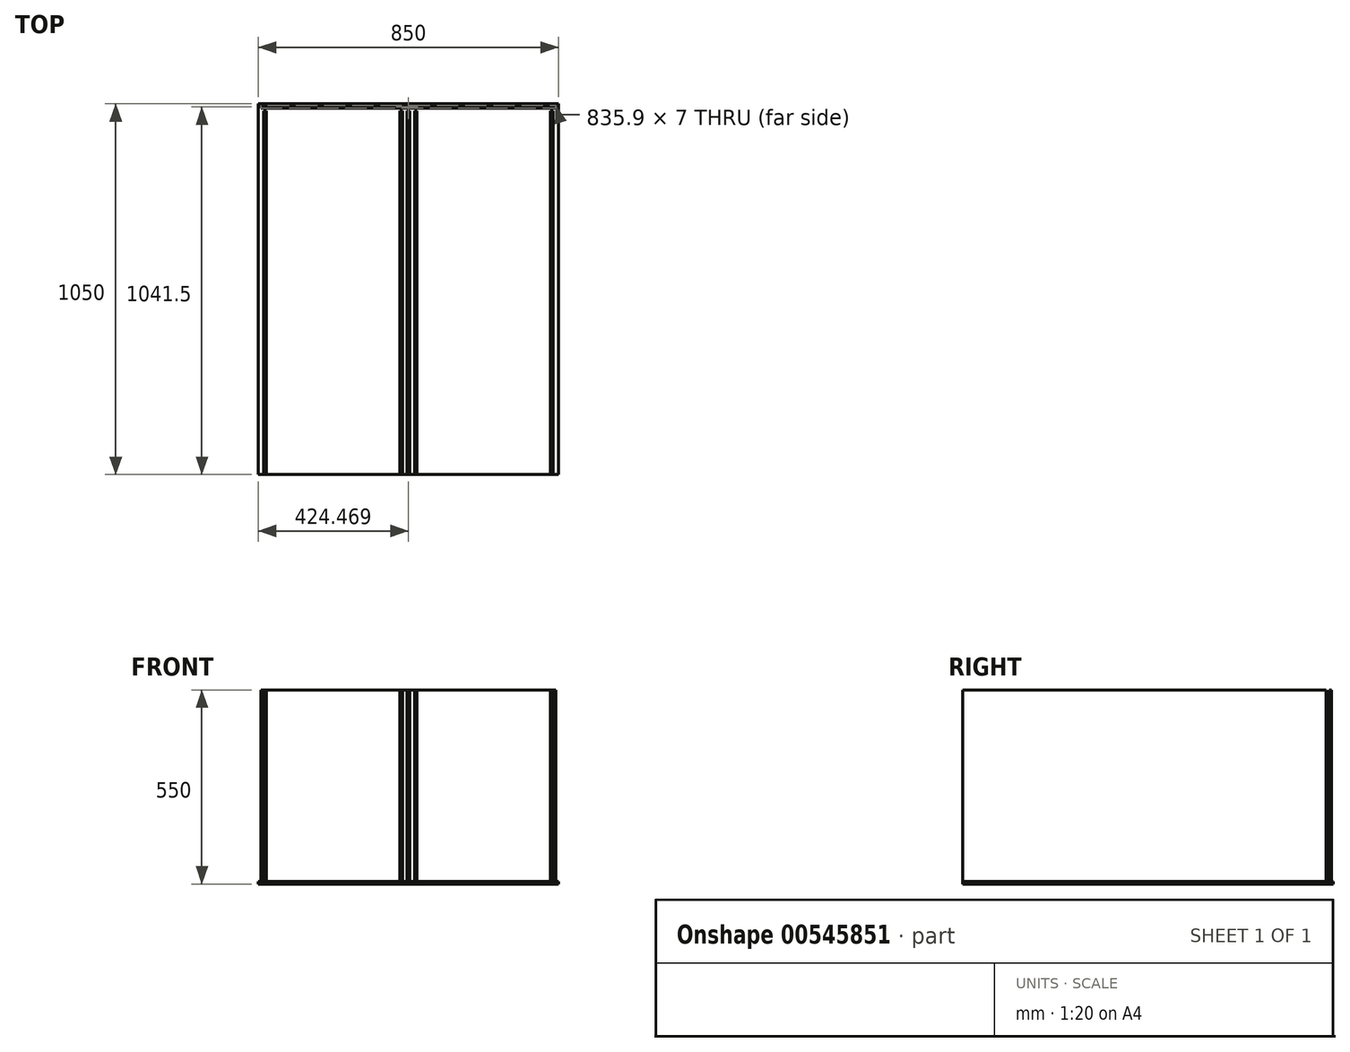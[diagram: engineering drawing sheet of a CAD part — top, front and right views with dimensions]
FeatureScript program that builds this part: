
annotation { "Feature Type Name" : "Feature", "Feature Type Description" : "" }
export const myFeature = defineFeature(function(context is Context, id is Id, definition is map)
    precondition{}
    {
        {
            var Q0;
            Q0=qCreatedBy(makeId("Top.planeOp"),FACE);
            var sketch = newSketch(context, id + "F0", { "sketchPlane" : qUnion([Q0])});
            skLineSegment(sketch, "E0", {"start": v(0, 0) * mm, "end": v(0, -1700) * mm, "construction": true});
            skLineSegment(sketch, "E1", {"start": v(0, -1700) * mm, "end": v(-425, -1700) * mm, "construction": true});
            skLineSegment(sketch, "E2", {"start": v(-675, 0) * mm, "end": v(0, 0) * mm, "construction": true});
            skLineSegment(sketch, "E3", {"start": v(-675, -1200) * mm, "end": v(-675, -1700) * mm, "construction": true});
            skLineSegment(sketch, "E4", {"start": v(-675, -1700) * mm, "end": v(-425, -1700) * mm, "construction": true});
            skLineSegment(sketch, "E5.MirrorCS", {"start": v(675, 0) * mm, "end": v(0, 0) * mm, "construction": true});
            skLineSegment(sketch, "E6.MirrorCS", {"start": v(0, -1700) * mm, "end": v(425, -1700) * mm, "construction": true});
            skLineSegment(sketch, "E7", {"start": v(-425, -1700) * mm, "end": v(-675, -1200) * mm, "construction": true});
            skLineSegment(sketch, "E8", {"start": v(675, 0) * mm, "end": v(675, -1200) * mm, "construction": true});
            skLineSegment(sketch, "E9", {"start": v(425, -1700) * mm, "end": v(-425, -1700) * mm});
            skLineSegment(sketch, "E10", {"start": v(675, -1200) * mm, "end": v(425, -1700) * mm, "construction": true});
            skLineSegment(sketch, "E11", {"start": v(-675, -1200) * mm, "end": v(-675, 0) * mm, "construction": true});
            skLineSegment(sketch, "E12", {"start": v(-425, -650) * mm, "end": v(0, -650) * mm, "construction": true});
            skLineSegment(sketch, "E13.MirrorCS", {"start": v(425, -650) * mm, "end": v(0, -650) * mm, "construction": true});
            skLineSegment(sketch, "E14", {"start": v(-425, -650) * mm, "end": v(-425, -1700) * mm, "construction": true});
            skLineSegment(sketch, "E15", {"start": v(425, -650) * mm, "end": v(425, -1700) * mm, "construction": true});
            skLineSegment(sketch, "E16", {"start": v(-675, -1200) * mm, "end": v(-675, -1700) * mm});
            skLineSegment(sketch, "E17", {"start": v(-425, -1700) * mm, "end": v(-425, -1200) * mm});
            skLineSegment(sketch, "E18", {"start": v(-425, -1200) * mm, "end": v(-675, -1200) * mm});
            skLineSegment(sketch, "E19.MirrorCS", {"start": v(425, -1200) * mm, "end": v(675, -1200) * mm});
            skLineSegment(sketch, "E20.MirrorCS", {"start": v(425, -1700) * mm, "end": v(425, -1200) * mm});
            skLineSegment(sketch, "E21.MirrorCS", {"start": v(675, -1700) * mm, "end": v(425, -1700) * mm, "construction": true});
            skLineSegment(sketch, "E22.MirrorCS", {"start": v(675, -1200) * mm, "end": v(675, -1700) * mm, "construction": true});
            skLineSegment(sketch, "E23", {"start": v(-380, -800) * mm, "end": v(-380, -1630) * mm, "construction": true});
            skLineSegment(sketch, "E24", {"start": v(-30, -800) * mm, "end": v(-30, -1630) * mm, "construction": true});
            skLineSegment(sketch, "E25", {"start": v(-380, -800) * mm, "end": v(-30, -800) * mm, "construction": true});
            skLineSegment(sketch, "E26", {"start": v(-380, -1630) * mm, "end": v(-30, -1630) * mm, "construction": true});
            skLineSegment(sketch, "E27.MirrorCS", {"start": v(380, -800) * mm, "end": v(30, -800) * mm, "construction": true});
            skLineSegment(sketch, "E28.MirrorCS", {"start": v(30, -800) * mm, "end": v(30, -1630) * mm, "construction": true});
            skLineSegment(sketch, "E29.bottom", {"start": v(-24, -670) * mm, "end": v(-17, -670) * mm});
            skLineSegment(sketch, "E29.top", {"start": v(-24, -1700) * mm, "end": v(-17, -1700) * mm});
            skLineSegment(sketch, "E29.left", {"start": v(-17, -670) * mm, "end": v(-17, -1700) * mm});
            skLineSegment(sketch, "E29.right", {"start": v(-24, -670) * mm, "end": v(-24, -1700) * mm});
            skLineSegment(sketch, "E30.bottom", {"start": v(-403, -1700) * mm, "end": v(-410, -1700) * mm});
            skLineSegment(sketch, "E30.top", {"start": v(-403, -670) * mm, "end": v(-410, -670) * mm});
            skLineSegment(sketch, "E30.left", {"start": v(-403, -1700) * mm, "end": v(-403, -670) * mm});
            skLineSegment(sketch, "E30.right", {"start": v(-410, -1700) * mm, "end": v(-410, -670) * mm});
            skLineSegment(sketch, "E31.bottom", {"start": v(-418.48, -662) * mm, "end": v(417.42, -662) * mm});
            skLineSegment(sketch, "E31.top", {"start": v(-418.48, -655) * mm, "end": v(417.42, -655) * mm});
            skLineSegment(sketch, "E31.left", {"start": v(-418.48, -662) * mm, "end": v(-418.48, -655) * mm});
            skLineSegment(sketch, "E31.right", {"start": v(417.42, -662) * mm, "end": v(417.42, -655) * mm});
            skLineSegment(sketch, "E32.MirrorCS", {"start": v(17, -670) * mm, "end": v(17, -1700) * mm});
            skLineSegment(sketch, "E33.MirrorCS", {"start": v(24, -670) * mm, "end": v(24, -1700) * mm});
            skLineSegment(sketch, "E34.MirrorCS", {"start": v(24, -670) * mm, "end": v(17, -670) * mm});
            skLineSegment(sketch, "E35.MirrorCS", {"start": v(403, -670) * mm, "end": v(410, -670) * mm});
            skLineSegment(sketch, "E36.MirrorCS", {"start": v(403, -1700) * mm, "end": v(403, -670) * mm});
            skLineSegment(sketch, "E37.MirrorCS", {"start": v(410, -1700) * mm, "end": v(410, -670) * mm});
            skLineSegment(sketch, "E38.bottom", {"start": v(-3.5, -1700) * mm, "end": v(3.5, -1700) * mm});
            skLineSegment(sketch, "E38.top", {"start": v(-3.5, -670) * mm, "end": v(3.5, -670) * mm});
            skLineSegment(sketch, "E38.left", {"start": v(-3.5, -1700) * mm, "end": v(-3.5, -670) * mm});
            skLineSegment(sketch, "E38.right", {"start": v(3.5, -1700) * mm, "end": v(3.5, -670) * mm});
            skLineSegment(sketch, "E39.bottom", {"start": v(-425, -1700) * mm, "end": v(425, -1700) * mm});
            skLineSegment(sketch, "E39.top", {"start": v(-425, -650) * mm, "end": v(425, -650) * mm});
            skLineSegment(sketch, "E39.left", {"start": v(-425, -1700) * mm, "end": v(-425, -650) * mm});
            skLineSegment(sketch, "E39.right", {"start": v(425, -1700) * mm, "end": v(425, -650) * mm});
            skSolve(sketch);
        }
        {
            var Q0;
            Q0=makeQuery(id+"F0.imprint","IMPRINT",FACE,{"disambiguationData":[TD([[makeQuery(id+"F0.imprint","IMPRINT",EDGE,{"derivedFrom":sQuery(id+"F0.wireOp",EDGE,"E35.MirrorCS")}),-1.0]])]});
            var Q1;
            {var subQ0=sQuery(id+"F0.wireOp",EDGE,"E32.MirrorCS");Q1=makeQuery(id+"F0.imprint","IMPRINT",FACE,{"disambiguationData":[TD([[makeQuery(id+"F0.imprint","IMPRINT",EDGE,{"derivedFrom":subQ0}),1.0]])]});}
            var Q2;
            Q2=makeQuery(id+"F0.imprint","IMPRINT",FACE,{"disambiguationData":[TD([[makeQuery(id+"F0.imprint","IMPRINT",EDGE,{"derivedFrom":sQuery(id+"F0.wireOp",EDGE,"E38.top")}),-1.0]])]});
            var Q3;
            Q3=makeQuery(id+"F0.imprint","IMPRINT",FACE,{"disambiguationData":[TD([[makeQuery(id+"F0.imprint","IMPRINT",EDGE,{"derivedFrom":sQuery(id+"F0.wireOp",EDGE,"E29.bottom")}),-1.0]])]});
            var Q4;
            Q4=makeQuery(id+"F0.imprint","IMPRINT",FACE,{"disambiguationData":[TD([[makeQuery(id+"F0.imprint","IMPRINT",EDGE,{"derivedFrom":sQuery(id+"F0.wireOp",EDGE,"E30.top")}),1.0]])]});
            var Q5;
            Q5=makeQuery(id+"F0.imprint","IMPRINT",FACE,{"disambiguationData":[TD([[makeQuery(id+"F0.imprint","IMPRINT",EDGE,{"derivedFrom":sQuery(id+"F0.wireOp",EDGE,"E31.bottom")}),1.0]])]});
            extrude(context, id + "F1", {"entities" : qUnion([Q0, Q1, Q2, Q3, Q4, Q5]), "depth" : 550 * mm, "offsetDistance" : 25 * mm});
        }
        {
            var Q0;
            Q0 = qSketchRegion(id + "F0", true);
            extrude(context, id + "F2", {"entities" : qUnion([Q0]), "depth" : 7 * mm, "offsetDistance" : 25 * mm});
        }
    });
